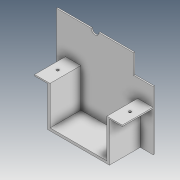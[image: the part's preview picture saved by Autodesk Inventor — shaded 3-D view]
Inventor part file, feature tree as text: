
AUTODESK INVENTOR PART (.ipt)
format: ipt  version: 2021 (Build 250183000, 183)  size: 234,496 bytes
history: native  units: in
note: dims shown in document units (in); Inventor stores cm internally (conversion verified against a paired STEP export)
features: extrude x14, sketch x14, other x1
ambient origin geometry x8: Origin, YZ Plane, XZ Plane, XY Plane, X Axis, Y Axis, Z Axis, Center Point
bodies: Body1 (feature_tree)
feature tree (29):
  other  "Sólido1"
  extrude  "Extrusão1"  Depth=1.1811in
  extrude  "Extrusão2"  Depth=0.2953in
  extrude  "Extrusão3"  Depth=0.0197in TaperAngle=0.0deg
  extrude  "Extrusão4"  Depth=0.0197in TaperAngle=0.0deg
  extrude  "Extrusão5"  Depth=0.1575in
  extrude  "Extrusão6"  Depth=0.7874in
  extrude  "Extrusão7"  Depth=0.374in
  extrude  "Extrusão8"  Depth=0.0394in
  extrude  "Extrusão9"  Depth=0.374in
  extrude  "Extrusão10"  Depth=0.6496in
  extrude  "Extrusão11"  Depth=0.0394in
  extrude  "Extrusão12"  Depth=0.0197in
  extrude  "Extrusão13"  Depth=0.4724in TaperAngle=0.0deg
  extrude  "Extrusão14"  Depth=0.4724in TaperAngle=0.0deg
  sketch  "Esboço1"  dims[d0=1.1811in d1=1.4331in]
  sketch  "Esboço2"  dims[d2=0.0197in d3=0.0in d4=0.2953in]
  sketch  "Esboço4"  dims[d5=0.1181in d6=0.0197in d7=0.0in]
  sketch  "Esboço5"  dims[d10=0.0276in d11=0.0197in d12=0.0in]
  sketch  "Esboço6"  dims[d13=0.1575in d14=0.1575in]
  sketch  "Esboço7"  dims[d15=0.2165in d16=0.7874in]
  sketch  "Esboço8"  dims[d17=0.0197in d18=0.0in d19=0.374in]
  sketch  "Esboço9"  dims[d20=0.1535in d21=0.0394in]
  sketch  "Esboço10"  dims[d22=0.0197in d23=0.0in d24=0.374in]
  sketch  "Esboço11"  dims[d25=0.1929in d26=0.6496in]
  sketch  "Esboço12"  dims[d27=0.0394in d28=0.0394in]
  sketch  "Esboço13"  dims[d29=0.0197in d30=0.0197in]
  sketch  "Esboço14"  dims[d31=0.0197in d32=0.4724in d33=0.0in]
  sketch  "Esboço15"  dims[d34=0.0197in d35=0.0in d36=0.4724in d37=0.0in d38=0.0787in d39=0.4724in d40=0.0in d41=0.0197in d42=0.1969in d43=0.0in d44=0.1969in d45=0.0in d46=0.1969in d47=0.0in d48=0.2362in d49=0.0394in d50=0.0394in d51=0.1969in d52=0.0in d53=0.0197in d54=0.0in]
